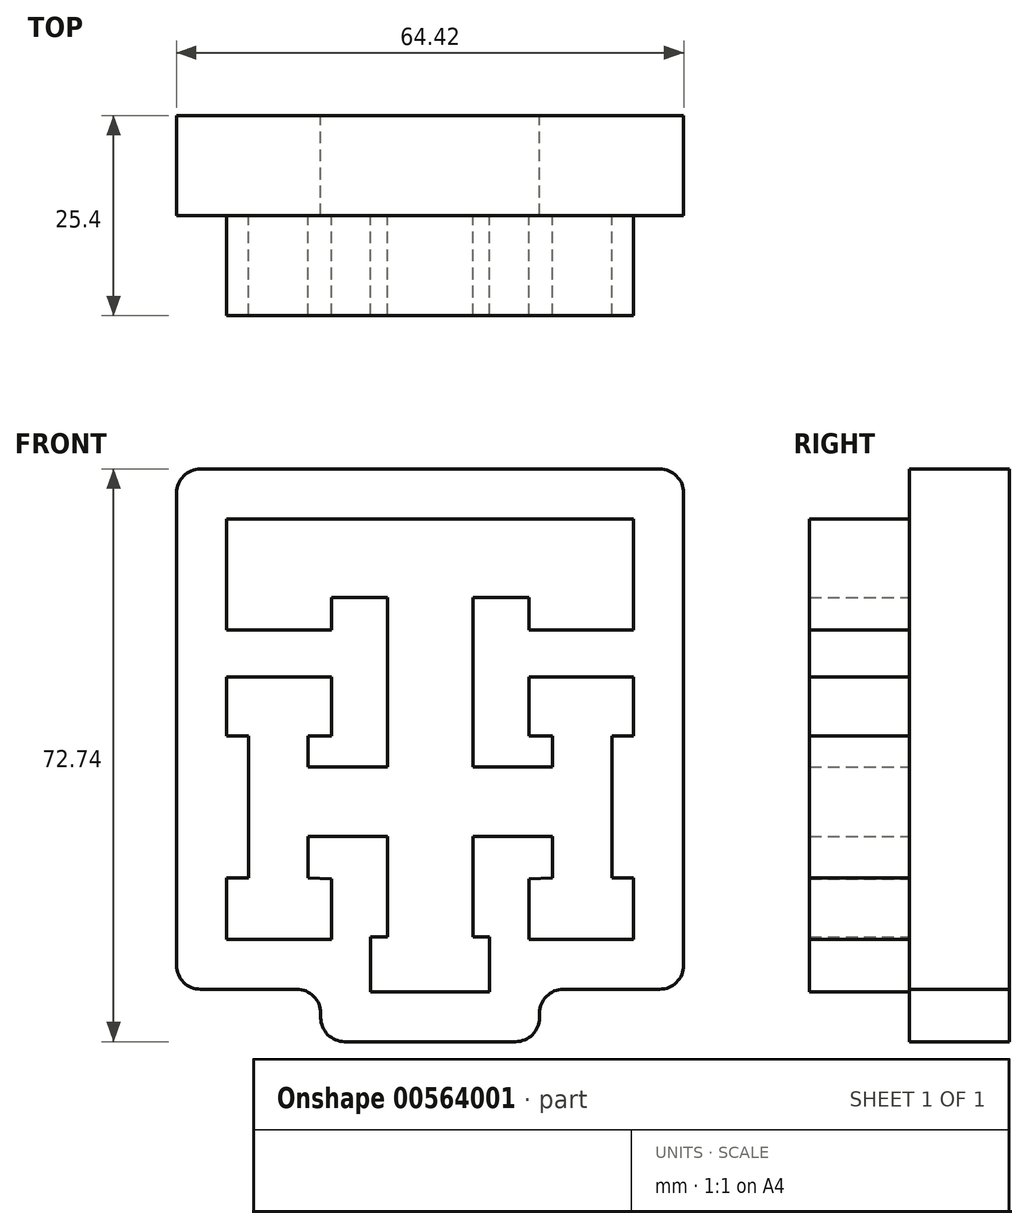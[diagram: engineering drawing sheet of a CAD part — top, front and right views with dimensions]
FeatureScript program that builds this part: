
annotation { "Feature Type Name" : "Feature", "Feature Type Description" : "" }
export const myFeature = defineFeature(function(context is Context, id is Id, definition is map)
    precondition{}
    {
        {
            var Q0;
            Q0=qCreatedBy(makeId("Front.planeOp"),FACE);
            var sketch = newSketch(context, id + "F0", { "sketchPlane" : qUnion([Q0])});
            skLineSegment(sketch, "E0", {"start": v(14.11, 50.57) * mm, "end": v(65.83, 50.57) * mm});
            skLineSegment(sketch, "E1", {"start": v(34.53, 40.58) * mm, "end": v(27.43, 40.58) * mm});
            skLineSegment(sketch, "E2", {"start": v(27.43, 40.58) * mm, "end": v(27.43, 36.47) * mm});
            skLineSegment(sketch, "E3", {"start": v(14.11, 50.57) * mm, "end": v(14.11, 36.47) * mm});
            skLineSegment(sketch, "E4", {"start": v(39.97, 50.57) * mm, "end": v(39.97, -13.35) * mm, "construction": true});
            skLineSegment(sketch, "E5.trimOffspring", {"start": v(27.43, 36.47) * mm, "end": v(14.11, 36.47) * mm});
            skPoint(sketch, "E6.start.orphan", {"position": v(65.83, 50.57) * mm});
            skLineSegment(sketch, "E7", {"start": v(14.11, 30.48) * mm, "end": v(27.43, 30.48) * mm});
            skLineSegment(sketch, "E8", {"start": v(14.11, -2.81) * mm, "end": v(27.43, -2.81) * mm});
            skLineSegment(sketch, "E9", {"start": v(14.11, 23) * mm, "end": v(16.89, 23) * mm});
            skLineSegment(sketch, "E10", {"start": v(16.89, 23) * mm, "end": v(16.89, 4.96) * mm});
            skLineSegment(sketch, "E11", {"start": v(16.89, 4.96) * mm, "end": v(14.11, 4.96) * mm});
            skLineSegment(sketch, "E12", {"start": v(27.43, 4.85) * mm, "end": v(24.43, 4.96) * mm});
            skLineSegment(sketch, "E13", {"start": v(24.43, 4.96) * mm, "end": v(24.43, 10.28) * mm});
            skLineSegment(sketch, "E14", {"start": v(34.53, 40.58) * mm, "end": v(34.53, 19.05) * mm});
            skLineSegment(sketch, "E15", {"start": v(34.53, -2.48) * mm, "end": v(32.42, -2.48) * mm});
            skLineSegment(sketch, "E16", {"start": v(32.42, -2.48) * mm, "end": v(32.42, -9.47) * mm});
            skLineSegment(sketch, "E17", {"start": v(34.53, 19.05) * mm, "end": v(24.43, 19.05) * mm});
            skLineSegment(sketch, "E18", {"start": v(34.53, 10.28) * mm, "end": v(24.43, 10.28) * mm});
            skPoint(sketch, "E19.orphan", {"position": v(14.11, -4.59) * mm});
            skLineSegment(sketch, "E20.trimOffspring", {"start": v(14.11, 4.96) * mm, "end": v(14.11, -2.81) * mm});
            skLineSegment(sketch, "E21.trimOffspring", {"start": v(27.43, 4.85) * mm, "end": v(27.43, -2.81) * mm});
            skLineSegment(sketch, "E22.trimOffspring", {"start": v(24.43, 19.05) * mm, "end": v(24.43, 23) * mm});
            skLineSegment(sketch, "E23.trimOffspring", {"start": v(34.53, 10.28) * mm, "end": v(34.53, -2.48) * mm});
            skLineSegment(sketch, "E24.trimOffspring", {"start": v(27.43, 30.48) * mm, "end": v(27.43, 23) * mm});
            skLineSegment(sketch, "E25.trimOffspring", {"start": v(24.43, 23) * mm, "end": v(27.43, 23) * mm});
            skLineSegment(sketch, "E26.trimOffspring", {"start": v(14.11, 30.48) * mm, "end": v(14.11, 23) * mm});
            skLineSegment(sketch, "E27.MirrorCS", {"start": v(63.05, 4.96) * mm, "end": v(65.83, 4.96) * mm});
            skLineSegment(sketch, "E28.MirrorCS", {"start": v(65.83, 23) * mm, "end": v(63.05, 23) * mm});
            skLineSegment(sketch, "E29.MirrorCS", {"start": v(45.4, -2.48) * mm, "end": v(47.52, -2.48) * mm});
            skLineSegment(sketch, "E30.MirrorCS", {"start": v(52.5, 40.58) * mm, "end": v(52.5, 36.47) * mm});
            skPoint(sketch, "E31.MirrorP", {"position": v(65.83, -4.59) * mm});
            skLineSegment(sketch, "E32.MirrorCS", {"start": v(52.5, 4.85) * mm, "end": v(55.5, 4.96) * mm});
            skLineSegment(sketch, "E33.MirrorCS", {"start": v(65.83, 50.57) * mm, "end": v(65.83, 36.47) * mm});
            skLineSegment(sketch, "E34.MirrorCS", {"start": v(63.05, 23) * mm, "end": v(63.05, 4.96) * mm});
            skLineSegment(sketch, "E35.MirrorCS", {"start": v(47.52, -2.48) * mm, "end": v(47.52, -9.47) * mm});
            skLineSegment(sketch, "E36.MirrorCS", {"start": v(45.4, 40.58) * mm, "end": v(45.4, 19.05) * mm});
            skLineSegment(sketch, "E37.MirrorCS", {"start": v(45.4, 40.58) * mm, "end": v(52.5, 40.58) * mm});
            skLineSegment(sketch, "E38.MirrorCS", {"start": v(45.4, 19.05) * mm, "end": v(55.5, 19.05) * mm});
            skLineSegment(sketch, "E39.MirrorCS", {"start": v(52.5, 36.47) * mm, "end": v(65.83, 36.47) * mm});
            skLineSegment(sketch, "E40.MirrorCS", {"start": v(65.83, 4.96) * mm, "end": v(65.83, -2.81) * mm});
            skLineSegment(sketch, "E41.MirrorCS", {"start": v(45.4, 10.28) * mm, "end": v(45.4, -2.48) * mm});
            skLineSegment(sketch, "E42.MirrorCS", {"start": v(52.5, 4.85) * mm, "end": v(52.5, -2.81) * mm});
            skLineSegment(sketch, "E43.MirrorCS", {"start": v(55.5, 23) * mm, "end": v(52.5, 23) * mm});
            skLineSegment(sketch, "E44.MirrorCS", {"start": v(65.83, 30.48) * mm, "end": v(52.5, 30.48) * mm});
            skLineSegment(sketch, "E45.MirrorCS", {"start": v(65.83, -2.81) * mm, "end": v(52.5, -2.81) * mm});
            skLineSegment(sketch, "E46.MirrorCS", {"start": v(52.5, 30.48) * mm, "end": v(52.5, 23) * mm});
            skLineSegment(sketch, "E47.MirrorCS", {"start": v(55.5, 19.05) * mm, "end": v(55.5, 23) * mm});
            skLineSegment(sketch, "E48.MirrorCS", {"start": v(55.5, 4.96) * mm, "end": v(55.5, 10.28) * mm});
            skLineSegment(sketch, "E49.MirrorCS", {"start": v(45.4, 10.28) * mm, "end": v(55.5, 10.28) * mm});
            skLineSegment(sketch, "E50.MirrorCS", {"start": v(65.83, 30.48) * mm, "end": v(65.83, 23) * mm});
            skLineSegment(sketch, "E51", {"start": v(32.42, -9.47) * mm, "end": v(47.52, -9.47) * mm});
            skSolve(sketch);
        }
        {
            var Q0;
            Q0 = qSketchRegion(id + "F0", true);
            extrude(context, id + "F1", {"entities" : qUnion([Q0]), "depth" : 25.4 * mm, "offsetDistance" : 25.4 * mm});
        }
        {
            var Q0;
            Q0=makeQuery(id+"F1.opExtrude","CAP_FACE",FACE,{"disambiguationData":[OSD([sQuery(id+"F0.wireOp",EDGE,"E0"),sQuery(id+"F0.wireOp",EDGE,"E1"),sQuery(id+"F0.wireOp",EDGE,"E2"),sQuery(id+"F0.wireOp",EDGE,"E3"),sQuery(id+"F0.wireOp",EDGE,"E5.trimOffspring"),sQuery(id+"F0.wireOp",EDGE,"E7"),sQuery(id+"F0.wireOp",EDGE,"E8"),sQuery(id+"F0.wireOp",EDGE,"E9"),sQuery(id+"F0.wireOp",EDGE,"E10"),sQuery(id+"F0.wireOp",EDGE,"E11"),sQuery(id+"F0.wireOp",EDGE,"E12"),sQuery(id+"F0.wireOp",EDGE,"E13"),sQuery(id+"F0.wireOp",EDGE,"E14"),sQuery(id+"F0.wireOp",EDGE,"E15"),sQuery(id+"F0.wireOp",EDGE,"E16"),sQuery(id+"F0.wireOp",EDGE,"E17"),sQuery(id+"F0.wireOp",EDGE,"E18"),sQuery(id+"F0.wireOp",EDGE,"E20.trimOffspring"),sQuery(id+"F0.wireOp",EDGE,"E21.trimOffspring"),sQuery(id+"F0.wireOp",EDGE,"E22.trimOffspring"),sQuery(id+"F0.wireOp",EDGE,"E23.trimOffspring"),sQuery(id+"F0.wireOp",EDGE,"E24.trimOffspring"),sQuery(id+"F0.wireOp",EDGE,"E25.trimOffspring"),sQuery(id+"F0.wireOp",EDGE,"E26.trimOffspring"),sQuery(id+"F0.wireOp",EDGE,"E27.MirrorCS"),sQuery(id+"F0.wireOp",EDGE,"E28.MirrorCS"),sQuery(id+"F0.wireOp",EDGE,"E29.MirrorCS"),sQuery(id+"F0.wireOp",EDGE,"E30.MirrorCS"),sQuery(id+"F0.wireOp",EDGE,"E32.MirrorCS"),sQuery(id+"F0.wireOp",EDGE,"E33.MirrorCS"),sQuery(id+"F0.wireOp",EDGE,"E34.MirrorCS"),sQuery(id+"F0.wireOp",EDGE,"E35.MirrorCS"),sQuery(id+"F0.wireOp",EDGE,"E36.MirrorCS"),sQuery(id+"F0.wireOp",EDGE,"E37.MirrorCS"),sQuery(id+"F0.wireOp",EDGE,"E38.MirrorCS"),sQuery(id+"F0.wireOp",EDGE,"E39.MirrorCS"),sQuery(id+"F0.wireOp",EDGE,"E40.MirrorCS"),sQuery(id+"F0.wireOp",EDGE,"E41.MirrorCS"),sQuery(id+"F0.wireOp",EDGE,"E42.MirrorCS"),sQuery(id+"F0.wireOp",EDGE,"E43.MirrorCS"),sQuery(id+"F0.wireOp",EDGE,"E44.MirrorCS"),sQuery(id+"F0.wireOp",EDGE,"E45.MirrorCS"),sQuery(id+"F0.wireOp",EDGE,"E46.MirrorCS"),sQuery(id+"F0.wireOp",EDGE,"E47.MirrorCS"),sQuery(id+"F0.wireOp",EDGE,"E48.MirrorCS"),sQuery(id+"F0.wireOp",EDGE,"E49.MirrorCS"),sQuery(id+"F0.wireOp",EDGE,"E50.MirrorCS"),sQuery(id+"F0.wireOp",EDGE,"E51")])],"isStart":true});
            var sketch = newSketch(context, id + "F2", { "sketchPlane" : qUnion([Q0])});
            skLineSegment(sketch, "E52.0", {"start": v(-7.76, 56.92) * mm, "end": v(-72.18, 56.92) * mm});
            skLineSegment(sketch, "E53.0", {"start": v(-72.18, 56.92) * mm, "end": v(-72.18, -9.16) * mm});
            skLineSegment(sketch, "E54.0", {"start": v(-72.18, -9.16) * mm, "end": v(-53.87, -9.16) * mm});
            skLineSegment(sketch, "E55.0", {"start": v(-53.87, -9.16) * mm, "end": v(-53.87, -15.82) * mm});
            skLineSegment(sketch, "E56.0", {"start": v(-26.07, -15.82) * mm, "end": v(-53.87, -15.82) * mm});
            skLineSegment(sketch, "E57.0", {"start": v(-26.07, -9.16) * mm, "end": v(-26.07, -15.82) * mm});
            skLineSegment(sketch, "E58.0", {"start": v(-7.76, -9.16) * mm, "end": v(-26.07, -9.16) * mm});
            skLineSegment(sketch, "E59.0", {"start": v(-7.76, 56.92) * mm, "end": v(-7.76, -9.16) * mm});
            skSolve(sketch);
        }
        {
            var Q0;
            Q0=makeQuery(id+"F2.imprint","IMPRINT",FACE,{"disambiguationData":[TD([[makeQuery(id+"F2.imprint","IMPRINT",EDGE,{"derivedFrom":sQuery(id+"F2.wireOp",EDGE,"E52.0")}),1.0]])]});
            extrude(context, id + "F3", {"entities" : qUnion([Q0]), "operationType" : NewBodyOperationType.ADD, "oppositeDirection" : true, "depth" : 12.7 * mm, "offsetDistance" : 25.4 * mm});
        }
        {
            var Q0;
            Q0=makeQuery(id+"F3.opExtrude","SWEPT_EDGE",EDGE,{"disambiguationData":[OSD([sQuery(id+"F2.wireOp",EDGE,"E58.0"),sQuery(id+"F2.wireOp",EDGE,"E59.0")])]});
            var Q1;
            Q1=makeQuery(id+"F3.opExtrude","SWEPT_EDGE",EDGE,{"disambiguationData":[OSD([sQuery(id+"F2.wireOp",EDGE,"E57.0"),sQuery(id+"F2.wireOp",EDGE,"E58.0")])]});
            var Q2;
            Q2=makeQuery(id+"F3.opExtrude","SWEPT_EDGE",EDGE,{"disambiguationData":[OSD([sQuery(id+"F2.wireOp",EDGE,"E56.0"),sQuery(id+"F2.wireOp",EDGE,"E57.0")])]});
            var Q3;
            Q3=makeQuery(id+"F3.opExtrude","SWEPT_EDGE",EDGE,{"disambiguationData":[OSD([sQuery(id+"F2.wireOp",EDGE,"E55.0"),sQuery(id+"F2.wireOp",EDGE,"E56.0")])]});
            var Q4;
            Q4=makeQuery(id+"F3.opExtrude","SWEPT_EDGE",EDGE,{"disambiguationData":[OSD([sQuery(id+"F2.wireOp",EDGE,"E54.0"),sQuery(id+"F2.wireOp",EDGE,"E55.0")])]});
            var Q5;
            Q5=makeQuery(id+"F3.opExtrude","SWEPT_EDGE",EDGE,{"disambiguationData":[OSD([sQuery(id+"F2.wireOp",EDGE,"E53.0"),sQuery(id+"F2.wireOp",EDGE,"E54.0")])]});
            var Q6;
            Q6=makeQuery(id+"F3.opExtrude","SWEPT_EDGE",EDGE,{"disambiguationData":[OSD([sQuery(id+"F2.wireOp",EDGE,"E52.0"),sQuery(id+"F2.wireOp",EDGE,"E53.0")])]});
            var Q7;
            Q7=makeQuery(id+"F3.opExtrude","SWEPT_EDGE",EDGE,{"disambiguationData":[OSD([sQuery(id+"F2.wireOp",EDGE,"E52.0"),sQuery(id+"F2.wireOp",EDGE,"E59.0")])]});
            fillet(context, id + "F4", {"entities" : qUnion([Q0, Q1, Q2, Q3, Q4, Q5, Q6, Q7]), "radius" : 3.05 * mm, "tangentPropagation" : true, "allowEdgeOverflow" : false});
        }
    });
